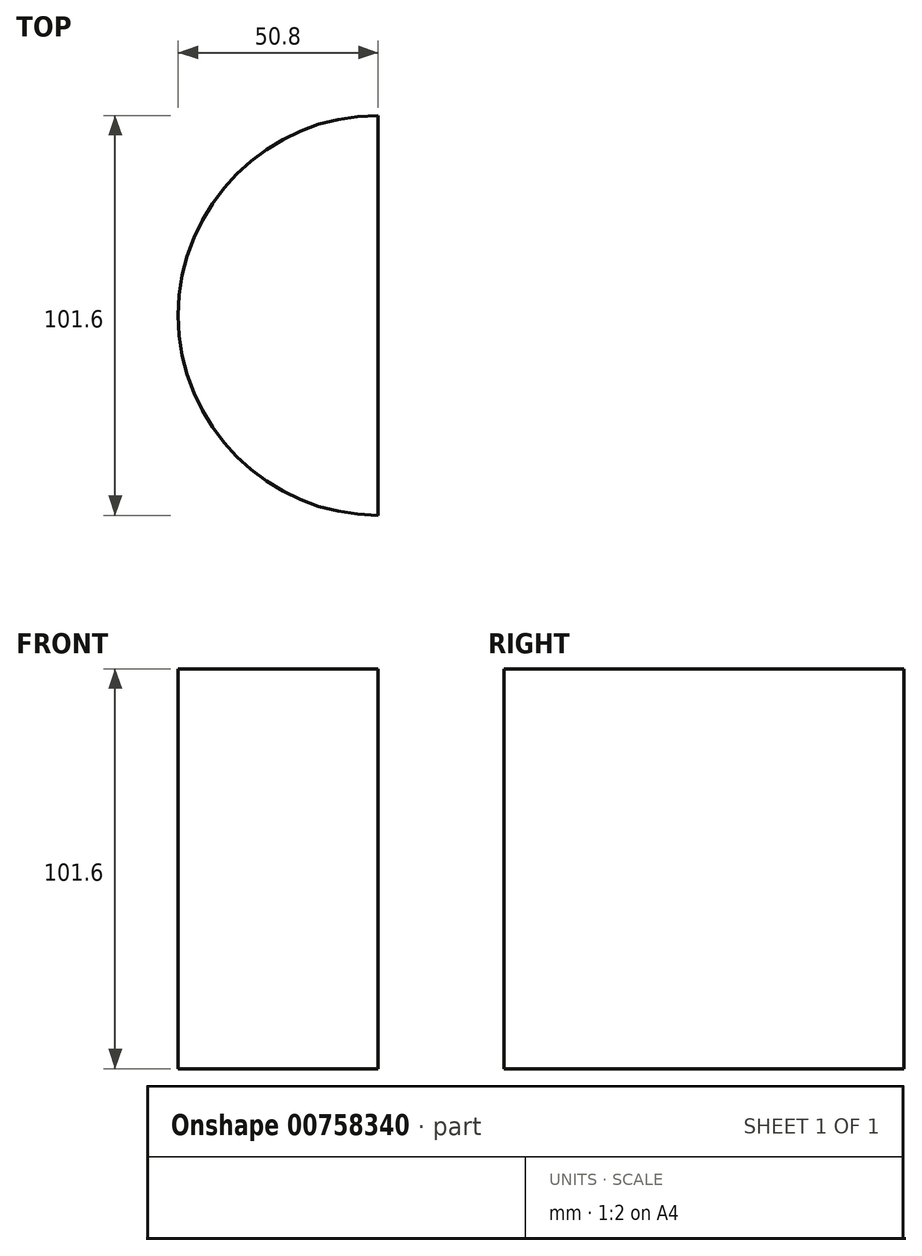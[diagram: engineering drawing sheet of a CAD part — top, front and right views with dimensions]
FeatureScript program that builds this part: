
annotation { "Feature Type Name" : "Feature", "Feature Type Description" : "" }
export const myFeature = defineFeature(function(context is Context, id is Id, definition is map)
    precondition{}
    {
        {
            var Q0;
            Q0=qCreatedBy(makeId("Top.planeOp"),FACE);
            var sketch = newSketch(context, id + "F0", { "sketchPlane" : qUnion([Q0])});
            skLineSegment(sketch, "E0", {"start": v(0, 0) * mm, "end": v(0, 101.6) * mm});
            skArc(sketch, "E1", {"start": v(0, 101.6) * mm, "mid": v(-50.8, 50.8) * mm, "end": v(0, 0) * mm});
            skSolve(sketch);
        }
        {
            var Q0;
            Q0=makeQuery(id+"F0.imprint","IMPRINT",FACE,{"disambiguationData":[TD([[makeQuery(id+"F0.imprint","IMPRINT",EDGE,{"derivedFrom":sQuery(id+"F0.wireOp",EDGE,"E0")}),1.0]])]});
            extrude(context, id + "F1", {"entities" : qUnion([Q0]), "depth" : 101.6 * mm, "offsetDistance" : 25.4 * mm});
        }
    });
